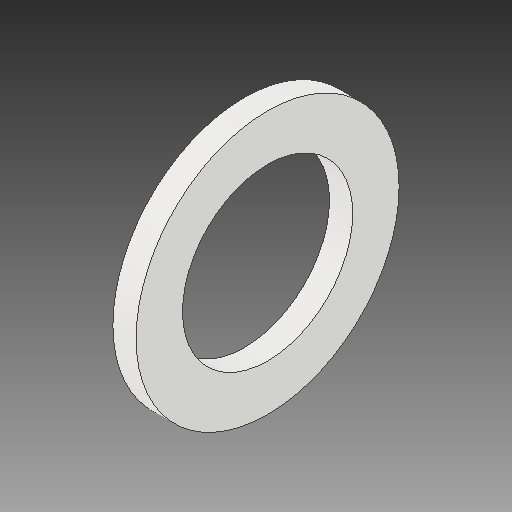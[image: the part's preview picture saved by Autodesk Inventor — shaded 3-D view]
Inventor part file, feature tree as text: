
AUTODESK INVENTOR PART (.ipt)
format: ipt  version: 2019 (Build 230136000, 136)  size: 108,032 bytes
history: native  units: mm
features: extrude x1, sketch x1
ambient origin geometry x8: Origin, YZ Plane, XZ Plane, XY Plane, X Axis, Y Axis, Z Axis, Center Point
bodies: Body1 (feature_tree)
feature tree (2):
  extrude  "Extrusion1"  Depth=3.0mm
  sketch  "Sketch1"  dims[d1=34.0mm d2=22.0mm d3=3.0mm d4=0.0mm]
